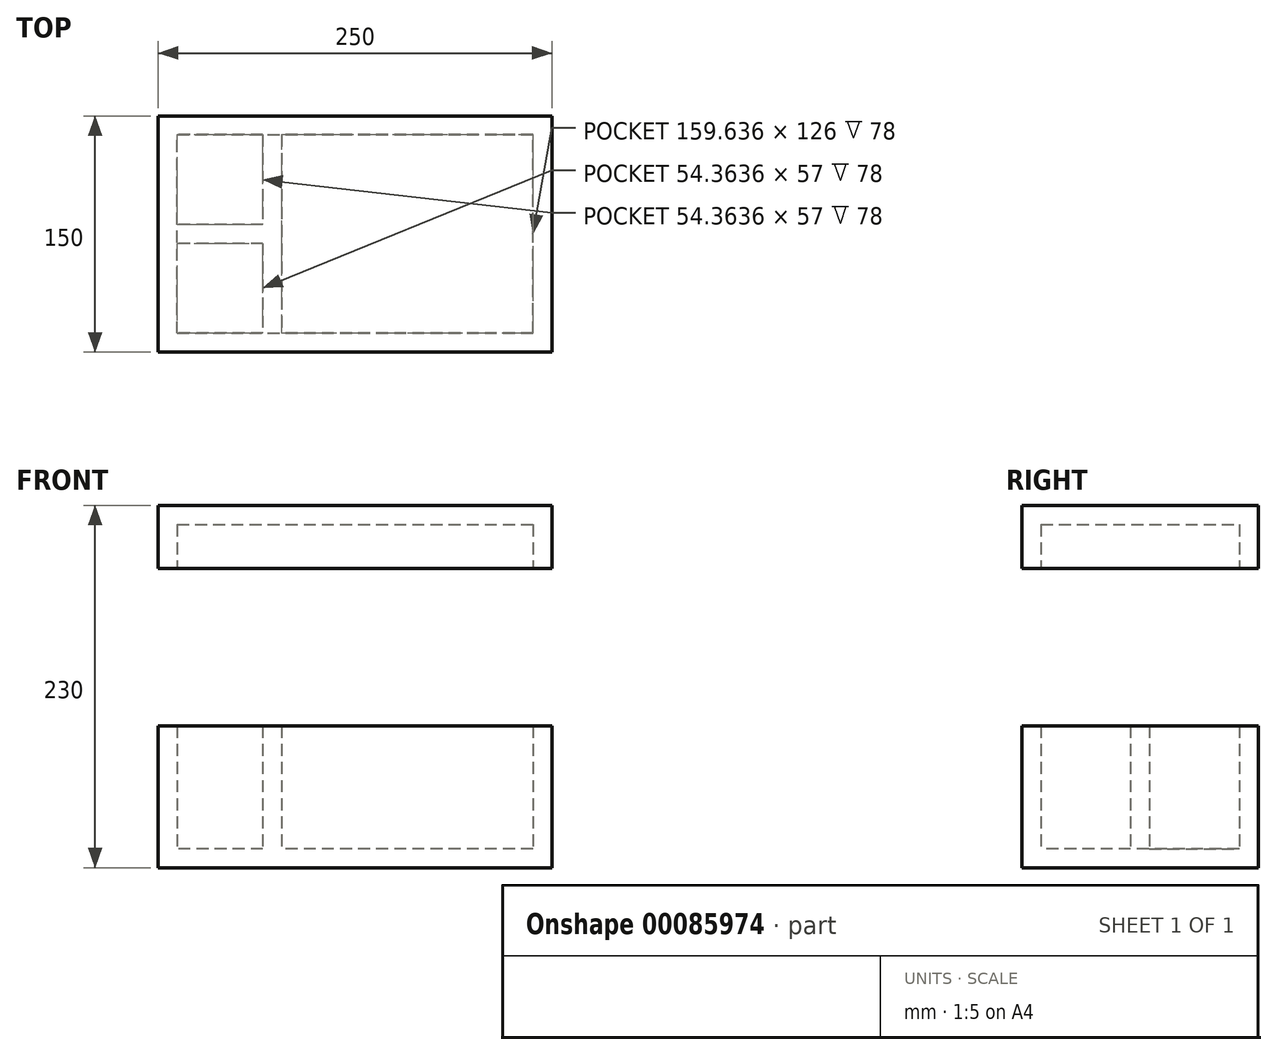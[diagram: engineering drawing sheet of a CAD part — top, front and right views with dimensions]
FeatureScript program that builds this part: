
annotation { "Feature Type Name" : "Feature", "Feature Type Description" : "" }
export const myFeature = defineFeature(function(context is Context, id is Id, definition is map)
    precondition{}
    {
        {
            var Q0;
            Q0=qCreatedBy(makeId("Top.planeOp"),FACE);
            var sketch = newSketch(context, id + "F0", { "sketchPlane" : qUnion([Q0])});
            skLineSegment(sketch, "E0.bottom", {"start": v(125, -75) * mm, "end": v(-125, -75) * mm});
            skLineSegment(sketch, "E0.top", {"start": v(125, 75) * mm, "end": v(-125, 75) * mm});
            skLineSegment(sketch, "E0.left", {"start": v(125, -75) * mm, "end": v(125, 75) * mm});
            skLineSegment(sketch, "E0.right", {"start": v(-125, -75) * mm, "end": v(-125, 75) * mm});
            skPoint(sketch, "E0.middle", {"position": v(0, 0) * mm});
            skSolve(sketch);
        }
        {
            var Q0;
            Q0=makeQuery(id+"F0.imprint","IMPRINT",FACE,{"disambiguationData":[TD([[makeQuery(id+"F0.imprint","IMPRINT",EDGE,{"derivedFrom":sQuery(id+"F0.wireOp",EDGE,"E0.bottom")}),-1.0]])]});
            extrude(context, id + "F1", {"entities" : qUnion([Q0]), "depth" : 90 * mm});
        }
        {
            var Q0;
            Q0=makeQuery(id+"F1.opExtrude","CAP_FACE",FACE,{"disambiguationData":[OSD([sQuery(id+"F0.wireOp",EDGE,"E0.bottom"),sQuery(id+"F0.wireOp",EDGE,"E0.top"),sQuery(id+"F0.wireOp",EDGE,"E0.left"),sQuery(id+"F0.wireOp",EDGE,"E0.right")])],"isStart":false});
            shell(context, id + "F2", {"entities" : qUnion([Q0]), "thickness" : 12 * mm});
        }
        {
            var Q0;
            Q0=makeQuery(id+"F2.opShell","OFFSET_FACE",FACE,{"disambiguationData":[OSD([sQuery(id+"F0.wireOp",EDGE,"E0.bottom"),sQuery(id+"F0.wireOp",EDGE,"E0.top"),sQuery(id+"F0.wireOp",EDGE,"E0.left"),sQuery(id+"F0.wireOp",EDGE,"E0.right")])]});
            var sketch = newSketch(context, id + "F3", { "sketchPlane" : qUnion([Q0])});
            skLineSegment(sketch, "E1.bottom", {"start": v(-46.64, 68.82) * mm, "end": v(-58.64, 68.82) * mm});
            skLineSegment(sketch, "E1.top", {"start": v(-46.64, -68.82) * mm, "end": v(-58.64, -68.82) * mm});
            skLineSegment(sketch, "E1.left", {"start": v(-46.64, 68.82) * mm, "end": v(-46.64, -68.82) * mm});
            skLineSegment(sketch, "E1.right", {"start": v(-58.64, 68.82) * mm, "end": v(-58.64, -68.82) * mm});
            skPoint(sketch, "E1.middle", {"position": v(-52.64, 0) * mm});
            skLineSegment(sketch, "E2.bottom", {"start": v(-53.04, 6) * mm, "end": v(-121.32, 6) * mm});
            skLineSegment(sketch, "E2.top", {"start": v(-53.04, -6) * mm, "end": v(-121.32, -6) * mm});
            skLineSegment(sketch, "E2.left", {"start": v(-53.04, 6) * mm, "end": v(-53.04, -6) * mm});
            skLineSegment(sketch, "E2.right", {"start": v(-121.32, 6) * mm, "end": v(-121.32, -6) * mm});
            skPoint(sketch, "E2.middle", {"position": v(-87.18, 0) * mm});
            skSolve(sketch);
        }
        {
            var Q0;
            {var subQ0=sQuery(id+"F3.wireOp",EDGE,"E2.bottom");var subQ1=sQuery(id+"F3.wireOp",EDGE,"E1.right");var subQ2=makeQuery(id+"F3.imprint","INTERSECT",VERTEX,{"derivedFrom":[subQ1,subQ0]});Q0=makeQuery(id+"F3.imprint","IMPRINT",FACE,{"disambiguationData":[TD([[makeQuery(id+"F3.imprint","IMPRINT",EDGE,{"disambiguationData":[TD([[subQ2,-1.0]])],"derivedFrom":subQ1}),-1.0]])]});}
            var Q1;
            {var subQ0=sQuery(id+"F3.wireOp",EDGE,"E2.left");Q1=makeQuery(id+"F3.imprint","IMPRINT",FACE,{"disambiguationData":[TD([[makeQuery(id+"F3.imprint","IMPRINT",EDGE,{"derivedFrom":subQ0}),1.0]])]});}
            var Q2;
            {var subQ5=sQuery(id+"F3.wireOp",EDGE,"E2.left");Q2=makeQuery(id+"F3.imprint","IMPRINT",FACE,{"disambiguationData":[TD([[makeQuery(id+"F3.imprint","IMPRINT",EDGE,{"derivedFrom":subQ5}),-1.0]])]});}
            extrude(context, id + "F4", {"entities" : qUnion([Q0, Q1, Q2]), "operationType" : NewBodyOperationType.ADD, "depth" : 78 * mm});
        }
        {
            var Q0;
            {var subQ0=sQuery(id+"F0.wireOp",EDGE,"E0.right");var subQ1=sQuery(id+"F0.wireOp",EDGE,"E0.top");var subQ2=sQuery(id+"F0.wireOp",EDGE,"E0.bottom");Q0=makeQuery(id+"F4.boolean.opBoolean","MERGE",FACE,{"derivedFrom":[makeQuery(id+"F1.opExtrude","CAP_FACE",FACE,{"disambiguationData":[OSD([subQ2,subQ1,sQuery(id+"F0.wireOp",EDGE,"E0.left"),subQ0])],"isStart":false}),makeQuery(id+"F4.opExtrude","CAP_FACE",FACE,{"disambiguationData":[OSD([subQ2,subQ1,subQ0,sQuery(id+"F3.wireOp",EDGE,"E1.left"),sQuery(id+"F3.wireOp",EDGE,"E1.right"),sQuery(id+"F3.wireOp",EDGE,"E2.bottom"),sQuery(id+"F3.wireOp",EDGE,"E2.top")])],"isStart":false})]});}
            cPlane(context, id + "F5", {"entities" : qUnion([Q0]), "cplaneType" : CPlaneType.OFFSET, "offset" : 100 * mm, "width" : 150 * mm, "height" : 150 * mm});
        }
        {
            var Q0;
            Q0=qCreatedBy(id+"F5.planeOp",FACE);
            var sketch = newSketch(context, id + "F6", { "sketchPlane" : qUnion([Q0])});
            skLineSegment(sketch, "E3.bottom", {"start": v(-125, -75) * mm, "end": v(125, -75) * mm});
            skLineSegment(sketch, "E3.top", {"start": v(-125, 75) * mm, "end": v(125, 75) * mm});
            skLineSegment(sketch, "E3.left", {"start": v(-125, -75) * mm, "end": v(-125, 75) * mm});
            skLineSegment(sketch, "E3.right", {"start": v(125, -75) * mm, "end": v(125, 75) * mm});
            skPoint(sketch, "E3.middle", {"position": v(0, 0) * mm});
            skSolve(sketch);
        }
        {
            var Q0;
            Q0=makeQuery(id+"F6.imprint","IMPRINT",FACE,{"disambiguationData":[TD([[makeQuery(id+"F6.imprint","IMPRINT",EDGE,{"derivedFrom":sQuery(id+"F6.wireOp",EDGE,"E3.bottom")}),1.0]])]});
            extrude(context, id + "F7", {"entities" : qUnion([Q0]), "depth" : 40 * mm});
        }
        {
            var Q0;
            Q0=makeQuery(id+"F7.opExtrude","CAP_FACE",FACE,{"disambiguationData":[OSD([sQuery(id+"F6.wireOp",EDGE,"E3.bottom"),sQuery(id+"F6.wireOp",EDGE,"E3.top"),sQuery(id+"F6.wireOp",EDGE,"E3.left"),sQuery(id+"F6.wireOp",EDGE,"E3.right")])],"isStart":true});
            shell(context, id + "F8", {"entities" : qUnion([Q0]), "thickness" : 12 * mm});
        }
    });
